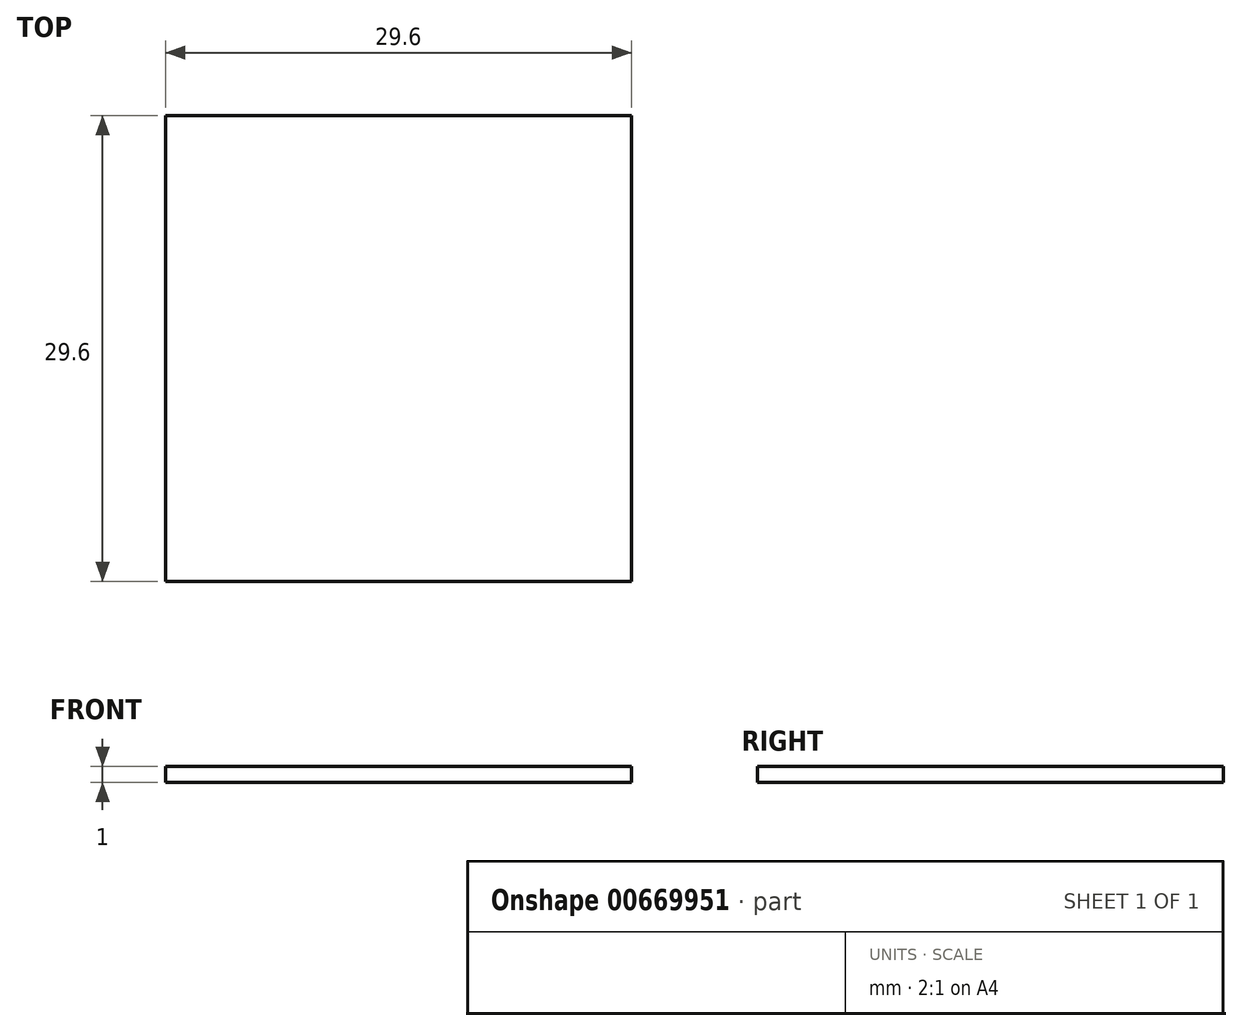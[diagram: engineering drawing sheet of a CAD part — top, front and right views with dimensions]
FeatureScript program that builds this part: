
annotation { "Feature Type Name" : "Feature", "Feature Type Description" : "" }
export const myFeature = defineFeature(function(context is Context, id is Id, definition is map)
    precondition{}
    {
        {
            var Q0;
            Q0=qCreatedBy(makeId("Top.planeOp"),FACE);
            var sketch = newSketch(context, id + "F0", { "sketchPlane" : qUnion([Q0])});
            skLineSegment(sketch, "E0.bottom", {"start": v(14.8, -14.8) * mm, "end": v(-14.8, -14.8) * mm});
            skLineSegment(sketch, "E0.top", {"start": v(14.8, 14.8) * mm, "end": v(-14.8, 14.8) * mm});
            skLineSegment(sketch, "E0.left", {"start": v(14.8, -14.8) * mm, "end": v(14.8, 14.8) * mm});
            skLineSegment(sketch, "E0.right", {"start": v(-14.8, -14.8) * mm, "end": v(-14.8, 14.8) * mm});
            skPoint(sketch, "E0.middle", {"position": v(0, 0) * mm});
            skSolve(sketch);
        }
        {
            var Q0;
            Q0=makeQuery(id+"F0.imprint","IMPRINT",FACE,{"disambiguationData":[TD([[makeQuery(id+"F0.imprint","IMPRINT",EDGE,{"derivedFrom":sQuery(id+"F0.wireOp",EDGE,"E0.bottom")}),-1.0]])]});
            extrude(context, id + "F1", {"entities" : qUnion([Q0]), "depth" : 1 * mm, "offsetDistance" : 25 * mm});
        }
    });
